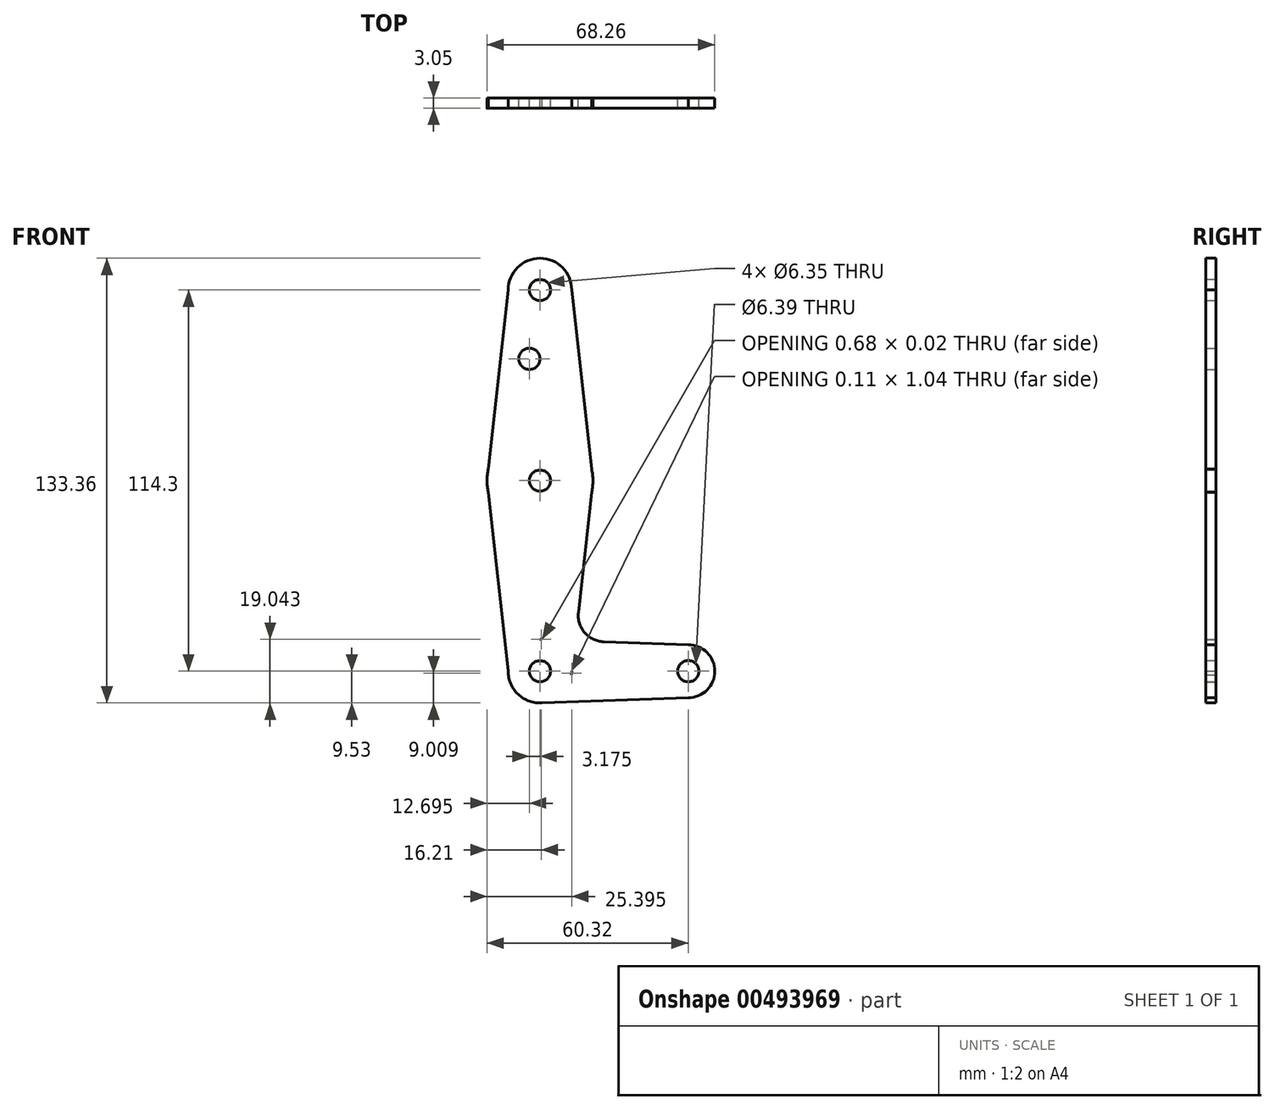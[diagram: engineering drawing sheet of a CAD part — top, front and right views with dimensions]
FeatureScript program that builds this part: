
annotation { "Feature Type Name" : "Feature", "Feature Type Description" : "" }
export const myFeature = defineFeature(function(context is Context, id is Id, definition is map)
    precondition{}
    {
        {
            var Q0;
            Q0=qCreatedBy(makeId("Front.planeOp"),FACE);
            var sketch = newSketch(context, id + "F0", { "sketchPlane" : qUnion([Q0])});
            skLineSegment(sketch, "E0", {"start": v(0, 0) * mm, "end": v(0, 114.3) * mm});
            skLineSegment(sketch, "E1", {"start": v(0, 0) * mm, "end": v(44.45, 0) * mm});
            skCircle(sketch, "E2", {"center": v(0, 114.3) * mm, "radius": 9.53 * mm});
            skCircle(sketch, "E3", {"center": v(0, 0) * mm, "radius": 9.53 * mm});
            skCircle(sketch, "E4", {"center": v(44.45, 0) * mm, "radius": 7.94 * mm});
            skCircle(sketch, "E5", {"center": v(0, 57.15) * mm, "radius": 15.88 * mm});
            skLineSegment(sketch, "E6", {"start": v(-9.52, 0) * mm, "end": v(-15.88, 57.15) * mm});
            skLineSegment(sketch, "E7", {"start": v(-15.88, 57.15) * mm, "end": v(-9.53, 114.3) * mm});
            skLineSegment(sketch, "E8", {"start": v(9.53, 114.3) * mm, "end": v(15.88, 57.15) * mm});
            skLineSegment(sketch, "E9", {"start": v(15.88, 57.15) * mm, "end": v(11.53, 17.66) * mm});
            skLineSegment(sketch, "E10", {"start": v(0, 9.52) * mm, "end": v(0.68, 9.5) * mm});
            skLineSegment(sketch, "E11", {"start": v(0, -9.52) * mm, "end": v(44.45, -7.94) * mm});
            skCircle(sketch, "E12", {"center": v(0, 114.3) * mm, "radius": 3.18 * mm});
            skCircle(sketch, "E13", {"center": v(0, 57.15) * mm, "radius": 3.18 * mm});
            skCircle(sketch, "E14", {"center": v(0, 0) * mm, "radius": 3.18 * mm});
            skCircle(sketch, "E15", {"center": v(44.45, 0) * mm, "radius": 3.2 * mm});
            skCircle(sketch, "E16", {"center": v(-3.18, 93.68) * mm, "radius": 3.18 * mm});
            skLineSegment(sketch, "E17.trimOffspring", {"start": v(19.15, 8.84) * mm, "end": v(44.45, 7.94) * mm});
            skLineSegment(sketch, "E18.trimOffspring", {"start": v(9.58, 0) * mm, "end": v(9.47, -1.04) * mm});
            skPoint(sketch, "E19.visualSharp", {"position": v(10.59, 9.15) * mm});
            skArc(sketch, "E19.filletArc", {"start": v(11.53, 17.66) * mm, "mid": v(13.41, 11.59) * mm, "end": v(19.15, 8.84) * mm});
            skSolve(sketch);
        }
        {
            var Q0;
            Q0 = qSketchRegion(id + "F0", true);
            var Q1;
            {var subQ0=sQuery(id+"F0.wireOp",EDGE,"E10");Q1=makeQuery(id+"F0.imprint","IMPRINT",FACE,{"disambiguationData":[TD([[makeQuery(id+"F0.imprint","IMPRINT",EDGE,{"derivedFrom":subQ0}),-1.0]])]});}
            extrude(context, id + "F1", {"entities" : qUnion([Q0, Q1]), "depth" : 3.05 * mm});
        }
    });
